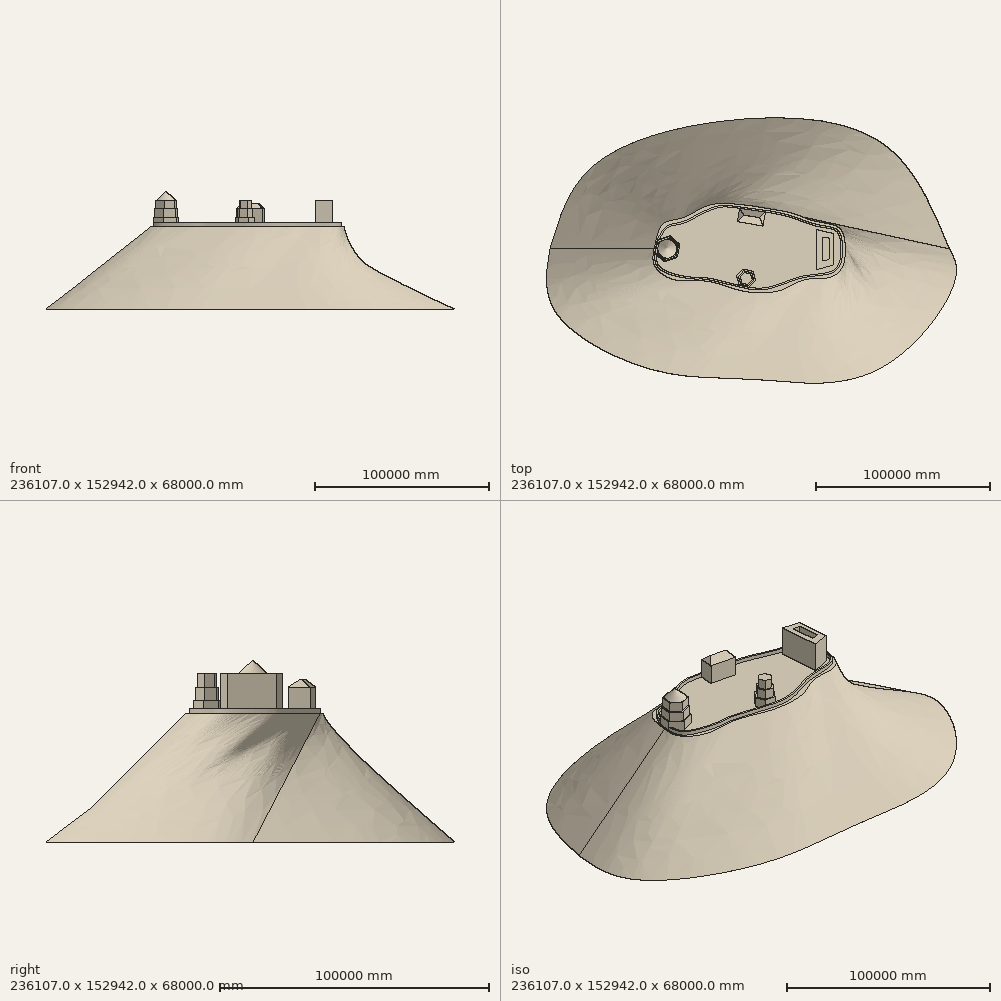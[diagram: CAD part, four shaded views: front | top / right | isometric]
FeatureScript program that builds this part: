
annotation { "Feature Type Name" : "Feature", "Feature Type Description" : "" }
export const myFeature = defineFeature(function(context is Context, id is Id, definition is map)
    precondition{}
    {
        {
            var Q0;
            Q0=qCreatedBy(makeId("Top.planeOp"),FACE);
            var sketch = newSketch(context, id + "F0", { "sketchPlane" : qUnion([Q0])});
            skFitSpline(sketch, "E0", {"points": [v(-115000, 0) * mm, v(-89790.23, 47800.29) * mm, v(0, 75000) * mm, v(78228.6, 59379.3) * mm, v(115000, 0) * mm], "startDerivative": vector(72130.1, 245823.46) * mm, "endDerivative": vector(117280.33, -283439.38) * mm});
            skFitSpline(sketch, "E1", {"points": [v(-115000, 0) * mm, v(-112209.16, -35716.4) * mm, v(-53821.4, -70207.06) * mm, v(0, -75000) * mm, v(72808.62, -70207.06) * mm, v(118631.94, -16746.53) * mm, v(115000, 0) * mm], "startDerivative": vector(-45187.79, -261735.86) * mm, "endDerivative": vector(-79154.57, 142787.81) * mm});
            skSolve(sketch);
        }
        {
            var Q0;
            Q0=qCreatedBy(makeId("Top.planeOp"),FACE);
            cPlane(context, id + "F1", {"entities" : qUnion([Q0]), "cplaneType" : CPlaneType.OFFSET, "offset" : 48000 * mm, "width" : 150 * mm, "height" : 150 * mm});
        }
        {
            var Q0;
            Q0=qCreatedBy(id+"F1.planeOp",FACE);
            var sketch = newSketch(context, id + "F2", { "sketchPlane" : qUnion([Q0])});
            skFitSpline(sketch, "E2", {"points": [v(0, 25000) * mm, v(-23615.07, 25000) * mm, v(-37680.98, 18064.81) * mm, v(-49445.19, 14484.4) * mm, v(-55000, 0) * mm], "startDerivative": vector(-85644.23, 10195.07) * mm, "endDerivative": vector(-13941.06, -73239.33) * mm});
            skFitSpline(sketch, "E3", {"points": [v(-55000, 0) * mm, v(-55000, -9189.99) * mm, v(-43801.45, -17724.95) * mm, v(-26596.06, -18402.32) * mm, v(-11016.37, -22331.11) * mm, v(0, -25000) * mm, v(18246.34, -23821.34) * mm, v(32200.32, -17724.95) * mm, v(46696.2, -16370.2) * mm, v(53605.45, -10138.32) * mm, v(55000, 0) * mm, v(51844.26, 11808.72) * mm, v(37212.9, 16008.46) * mm, v(25697.5, 20208.2) * mm, v(9846.85, 23324.13) * mm, v(0, 25000) * mm], "startDerivative": vector(-35298.95, -167696.15) * mm, "endDerivative": vector(-155833.8, 28078.38) * mm});
            skSolve(sketch);
        }
        {
            var Q0;
            Q0=makeQuery(id+"F0.imprint","IMPRINT",FACE,{"disambiguationData":[TD([[makeQuery(id+"F0.imprint","IMPRINT",EDGE,{"derivedFrom":sQuery(id+"F0.wireOp",EDGE,"E0")}),-1.0]])]});
            var Q1;
            Q1=makeQuery(id+"F2.imprint","IMPRINT",FACE,{"disambiguationData":[TD([[makeQuery(id+"F2.imprint","IMPRINT",EDGE,{"derivedFrom":sQuery(id+"F2.wireOp",EDGE,"E2")}),1.0]])]});
            loft(context, id + "F3", {"sheetProfilesArray" : [{ "sheetProfileEntities" : qUnion([Q0]) }, { "sheetProfileEntities" : qUnion([Q1]) }]});
        }
        {
            var Q0;
            Q0=makeQuery(id+"F3.opLoft","CAP_FACE",FACE,{"disambiguationData":[OSD([makeQuery(id+"F2.imprint","IMPRINT",FACE,{"disambiguationData":[TD([[makeQuery(id+"F2.imprint","IMPRINT",EDGE,{"derivedFrom":sQuery(id+"F2.wireOp",EDGE,"E2")}),1.0]])]})])],"isStart":true});
            var sketch = newSketch(context, id + "F4", { "sketchPlane" : qUnion([Q0])});
            skLineSegment(sketch, "E4", {"start": v(0, 0) * mm, "end": v(-55000, 0) * mm});
            skLineSegment(sketch, "E5", {"start": v(-55000, 0) * mm, "end": v(-47500, 0) * mm});
            skCircle(sketch, "E6.cCircle", {"center": v(-47500, 0) * mm, "radius": 6664.28 * mm, "construction": true});
            skLineSegment(sketch, "E6.0", {"start": v(-54796.66, -2444.5) * mm, "end": v(-53265.33, 5096.84) * mm});
            skLineSegment(sketch, "E6.1", {"start": v(-53265.33, 5096.84) * mm, "end": v(-45968.67, 7541.35) * mm});
            skLineSegment(sketch, "E6.2", {"start": v(-45968.67, 7541.35) * mm, "end": v(-40203.34, 2444.5) * mm});
            skLineSegment(sketch, "E6.3", {"start": v(-40203.34, 2444.5) * mm, "end": v(-41734.67, -5096.84) * mm});
            skLineSegment(sketch, "E6.4", {"start": v(-41734.67, -5096.84) * mm, "end": v(-49031.33, -7541.35) * mm});
            skLineSegment(sketch, "E6.5", {"start": v(-49031.33, -7541.35) * mm, "end": v(-54796.66, -2444.5) * mm});
            skPoint(sketch, "E6.0.midPoint", {"position": v(-54031, 1326.17) * mm});
            skSolve(sketch);
        }
        {
            var Q0;
            {var subQ0=sQuery(id+"F4.wireOp",EDGE,"E6.4");Q0=makeQuery(id+"F4.imprint","IMPRINT",FACE,{"disambiguationData":[TD([[makeQuery(id+"F4.imprint","IMPRINT",EDGE,{"derivedFrom":subQ0}),-1.0]])]});}
            var Q1;
            {var subQ0=sQuery(id+"F4.wireOp",EDGE,"E6.1");Q1=makeQuery(id+"F4.imprint","IMPRINT",FACE,{"disambiguationData":[TD([[makeQuery(id+"F4.imprint","IMPRINT",EDGE,{"derivedFrom":subQ0}),-1.0]])]});}
            extrude(context, id + "F5", {"entities" : qUnion([Q0, Q1]), "operationType" : NewBodyOperationType.ADD, "depth" : 5000 * mm});
        }
        {
            var Q0;
            Q0=makeQuery(id+"F5.opExtrude","CAP_FACE",FACE,{"disambiguationData":[OSD([sQuery(id+"F4.wireOp",EDGE,"E6.0"),sQuery(id+"F4.wireOp",EDGE,"E6.1"),sQuery(id+"F4.wireOp",EDGE,"E6.2"),sQuery(id+"F4.wireOp",EDGE,"E6.3"),sQuery(id+"F4.wireOp",EDGE,"E6.4"),sQuery(id+"F4.wireOp",EDGE,"E6.5")])],"isStart":false});
            var sketch = newSketch(context, id + "F6", { "sketchPlane" : qUnion([Q0])});
            skCircle(sketch, "E7.cCircle", {"center": v(-47581.15, 0) * mm, "radius": 6138.92 * mm, "construction": true});
            skLineSegment(sketch, "E7.0", {"start": v(-40859.7, 2251.8) * mm, "end": v(-42270.31, -4695.05) * mm});
            skLineSegment(sketch, "E7.1", {"start": v(-42270.31, -4695.05) * mm, "end": v(-48991.76, -6946.84) * mm});
            skLineSegment(sketch, "E7.2", {"start": v(-48991.76, -6946.84) * mm, "end": v(-54302.6, -2251.8) * mm});
            skLineSegment(sketch, "E7.3", {"start": v(-54302.6, -2251.8) * mm, "end": v(-52891.99, 4695.05) * mm});
            skLineSegment(sketch, "E7.4", {"start": v(-52891.99, 4695.05) * mm, "end": v(-46170.54, 6946.84) * mm});
            skLineSegment(sketch, "E7.5", {"start": v(-46170.54, 6946.84) * mm, "end": v(-40859.7, 2251.8) * mm});
            skPoint(sketch, "E7.0.midPoint", {"position": v(-41565, -1221.63) * mm});
            skSolve(sketch);
        }
        {
            var Q0;
            Q0=makeQuery(id+"F6.imprint","IMPRINT",FACE,{"disambiguationData":[TD([[makeQuery(id+"F6.imprint","IMPRINT",EDGE,{"derivedFrom":sQuery(id+"F6.wireOp",EDGE,"E7.0")}),-1.0]])]});
            extrude(context, id + "F7", {"entities" : qUnion([Q0]), "operationType" : NewBodyOperationType.ADD, "depth" : 5000 * mm});
        }
        {
            var Q0;
            Q0=makeQuery(id+"F7.opExtrude","CAP_FACE",FACE,{"disambiguationData":[OSD([sQuery(id+"F6.wireOp",EDGE,"E7.0"),sQuery(id+"F6.wireOp",EDGE,"E7.1"),sQuery(id+"F6.wireOp",EDGE,"E7.2"),sQuery(id+"F6.wireOp",EDGE,"E7.3"),sQuery(id+"F6.wireOp",EDGE,"E7.4"),sQuery(id+"F6.wireOp",EDGE,"E7.5")])],"isStart":false});
            var sketch = newSketch(context, id + "F8", { "sketchPlane" : qUnion([Q0])});
            skCircle(sketch, "E8.cCircle", {"center": v(-47481.06, 0) * mm, "radius": 5420.52 * mm, "construction": true});
            skLineSegment(sketch, "E8.0", {"start": v(-41546.18, 1988.28) * mm, "end": v(-42791.71, -4145.61) * mm});
            skLineSegment(sketch, "E8.1", {"start": v(-42791.71, -4145.61) * mm, "end": v(-48726.6, -6133.9) * mm});
            skLineSegment(sketch, "E8.2", {"start": v(-48726.6, -6133.9) * mm, "end": v(-53415.94, -1988.28) * mm});
            skLineSegment(sketch, "E8.3", {"start": v(-53415.94, -1988.28) * mm, "end": v(-52170.4, 4145.61) * mm});
            skLineSegment(sketch, "E8.4", {"start": v(-52170.4, 4145.61) * mm, "end": v(-46235.52, 6133.9) * mm});
            skLineSegment(sketch, "E8.5", {"start": v(-46235.52, 6133.9) * mm, "end": v(-41546.18, 1988.28) * mm});
            skPoint(sketch, "E8.0.midPoint", {"position": v(-42168.95, -1078.67) * mm});
            skSolve(sketch);
        }
        {
            var Q0;
            Q0=makeQuery(id+"F8.imprint","IMPRINT",FACE,{"disambiguationData":[TD([[makeQuery(id+"F8.imprint","IMPRINT",EDGE,{"derivedFrom":sQuery(id+"F8.wireOp",EDGE,"E8.0")}),-1.0]])]});
            extrude(context, id + "F9", {"entities" : qUnion([Q0]), "operationType" : NewBodyOperationType.ADD, "depth" : 5000 * mm});
        }
        {
            var Q0;
            Q0=makeQuery(id+"F3.opLoft","CAP_FACE",FACE,{"disambiguationData":[OSD([makeQuery(id+"F2.imprint","IMPRINT",FACE,{"disambiguationData":[TD([[makeQuery(id+"F2.imprint","IMPRINT",EDGE,{"derivedFrom":sQuery(id+"F2.wireOp",EDGE,"E2")}),1.0]])]})])],"isStart":true});
            var sketch = newSketch(context, id + "F10", { "sketchPlane" : qUnion([Q0])});
            skFitSpline(sketch, "E9", {"points": [v(-54796.66, -2444.5) * mm, v(-54025.04, -8683.25) * mm, v(-48181.4, -13844.42) * mm, v(-32100.73, -17384.73) * mm, v(-26814.83, -17382.16) * mm, v(-12304.75, -20499.15) * mm, v(8976.7, -23401.16) * mm, v(28547.6, -17221.27) * mm, v(42950.2, -15071.63) * mm, v(51333.8, -10879.83) * mm, v(53375.96, 3092.84) * mm, v(50151.5, 11154) * mm, v(39510.77, 13841.05) * mm, v(28169.48, 17572.49) * mm, v(16848.58, 20860.28) * mm, v(-6824.2, 24518.8) * mm, v(-17915.3, 24712.72) * mm, v(-30172.03, 19637.67) * mm, v(-39173.06, 15424.42) * mm, v(-47216.54, 13222.04) * mm, v(-53265.33, 5096.84) * mm], "startDerivative": vector(81.44, -181720.02) * mm, "endDerivative": vector(-114550.78, -214633.23) * mm});
            skFitSpline(sketch, "E10.0", {"points": [v(-54801.66, -2444.5) * mm, v(-54801.56, -2681.12) * mm, v(-54801.35, -3154.36) * mm, v(-54795.16, -3861.88) * mm, v(-54777.24, -4564.68) * mm, v(-54741.7, -5260.36) * mm, v(-54682.7, -5946.56) * mm, v(-54609.07, -6508.49) * mm, v(-54532.55, -6950.9) * mm, v(-54465.62, -7278.85) * mm, v(-54388.42, -7602.64) * mm, v(-54300.2, -7921.97) * mm, v(-54216.9, -8184.11) * mm, v(-54144.02, -8391.3) * mm, v(-54086.15, -8545.38) * mm, v(-54024.97, -8698.13) * mm, v(-53960.4, -8849.5) * mm, v(-53892.4, -8999.5) * mm, v(-53797.13, -9197.68) * mm, v(-53669.3, -9442.02) * mm, v(-53501.63, -9729.84) * mm, v(-53319.4, -10012.33) * mm, v(-53056.66, -10381.94) * mm, v(-52690.43, -10830.86) * mm, v(-52188.2, -11349) * mm, v(-51715.49, -11764) * mm, v(-51303.68, -12086.1) * mm, v(-50977.72, -12322.8) * mm, v(-50634.37, -12554.64) * mm, v(-50273.35, -12781.7) * mm, v(-49894.37, -13004.02) * mm, v(-49497.15, -13221.65) * mm, v(-49081.4, -13434.63) * mm, v(-48646.85, -13643.03) * mm, v(-48193.2, -13846.89) * mm, v(-47720.17, -14046.26) * mm, v(-47229.17, -14241.03) * mm, v(-46721.66, -14431.1) * mm, v(-46199.08, -14616.36) * mm, v(-45662.88, -14796.7) * mm, v(-45114.5, -14972.02) * mm, v(-44555.37, -15142.2) * mm, v(-43986.94, -15307.16) * mm, v(-43218.58, -15519.97) * mm, v(-42242.1, -15772.34) * mm, v(-41056.25, -16052.52) * mm, v(-39867.87, -16309.17) * mm, v(-38688.5, -16541.42) * mm, v(-37529.72, -16748.42) * mm, v(-36590.83, -16899.15) * mm, v(-35861.56, -17006.26) * mm, v(-35326.97, -17079.73) * mm, v(-34806.2, -17146.24) * mm, v(-34300.66, -17205.7) * mm, v(-33811.82, -17257.96) * mm, v(-33341.12, -17302.96) * mm, v(-32965.19, -17334.29) * mm, v(-32674.95, -17355.6) * mm, v(-32462.71, -17369.7) * mm, v(-32290.52, -17379.87) * mm, v(-32155.67, -17387.05) * mm, v(-32056, -17391.95) * mm, v(-31957.82, -17396.37) * mm, v(-31828.8, -17401.66) * mm, v(-31671.02, -17407.15) * mm, v(-31486.94, -17412.09) * mm, v(-31248.13, -17416.6) * mm, v(-30961.29, -17418.7) * mm, v(-30633.34, -17416.5) * mm, v(-30319.24, -17410.5) * mm, v(-30016.6, -17401.67) * mm, v(-29723, -17390.97) * mm, v(-29436.02, -17379.36) * mm, v(-29059.02, -17363.91) * mm, v(-28685.65, -17350.44) * mm, v(-28306.27, -17342.75) * mm, v(-28016.32, -17340.84) * mm, v(-27768.16, -17343.23) * mm, v(-27564.52, -17348.03) * mm, v(-27408.92, -17353.18) * mm, v(-27250.16, -17360) * mm, v(-27114.97, -17367.2) * mm, v(-27004.94, -17373.9) * mm, v(-26921.43, -17379.42) * mm, v(-26836.91, -17385.46) * mm, v(-26751.33, -17392.01) * mm, v(-26664.69, -17399.1) * mm, v(-26547.76, -17409.23) * mm, v(-26399, -17423.18) * mm, v(-26216.4, -17441.96) * mm, v(-25967.52, -17469.66) * mm, v(-25646.51, -17509.2) * mm, v(-25245.96, -17564.23) * mm, v(-24830.59, -17626.6) * mm, v(-24257.72, -17719.16) * mm, v(-23507.27, -17851.88) * mm, v(-22556, -18036.23) * mm, v(-21558.25, -18243.55) * mm, v(-20518.28, -18471.73) * mm, v(-19440.35, -18718.67) * mm, v(-18328.7, -18982.24) * mm, v(-17187.6, -19260.34) * mm, v(-16021.31, -19550.84) * mm, v(-15031.94, -19801.5) * mm, v(-14232.1, -20006.14) * mm, v(-13628.57, -20161.39) * mm, v(-13123.05, -20292.03) * mm, v(-12717.34, -20397.17) * mm, v(-12412.47, -20476.3) * mm, v(-12107.1, -20555.69) * mm, v(-11699.3, -20661.8) * mm, v(-11188.4, -20794.8) * mm, v(-10573.53, -20954.48) * mm, v(-9751.5, -21166.91) * mm, v(-8720.05, -21430.4) * mm, v(-7476.91, -21739.57) * mm, v(-6229.2, -22038.04) * mm, v(-4977.76, -22322.12) * mm, v(-3723.4, -22588.1) * mm, v(-2466.96, -22832.27) * mm, v(-1209.27, -23050.94) * mm, v(48.85, -23240.41) * mm, v(1306.55, -23396.98) * mm, v(2563.01, -23516.95) * mm, v(3817.4, -23596.62) * mm, v(4860.31, -23626.34) * mm, v(5692.77, -23626.26) * mm, v(6316.08, -23613.8) * mm, v(6938.24, -23588.5) * mm, v(7455.68, -23556.33) * mm, v(7868.95, -23523.7) * mm, v(8178.56, -23495.72) * mm, v(8487.8, -23464.19) * mm, v(8745.19, -23434.9) * mm, v(8950.9, -23409.62) * mm, v(9156.48, -23383.11) * mm, v(9413.21, -23347.68) * mm, v(9720.88, -23301.59) * mm, v(10130.57, -23235.5) * mm, v(10641.67, -23144.4) * mm, v(11253.33, -23022.31) * mm, v(11863.33, -22888.2) * mm, v(12674.42, -22694.34) * mm, v(13684.02, -22425.75) * mm, v(14888.59, -22067.44) * mm, v(16086.05, -21679.2) * mm, v(17276.26, -21267.08) * mm, v(18459.07, -20837.15) * mm, v(19634.34, -20395.46) * mm, v(20801.91, -19948.07) * mm, v(21961.65, -19501.04) * mm, v(23113.4, -19060.42) * mm, v(24066.4, -18703.64) * mm, v(24824.66, -18427.48) * mm, v(25391.27, -18225.75) * mm, v(25955.76, -18030.17) * mm, v(26518.13, -17841.49) * mm, v(26984.98, -17690.64) * mm, v(27357.38, -17574.17) * mm, v(27636.14, -17489.02) * mm, v(27914.35, -17406.16) * mm, v(28192, -17325.69) * mm, v(28422.93, -17260.7) * mm, v(28607.4, -17210) * mm, v(28791.68, -17160.16) * mm, v(29021.68, -17099.46) * mm, v(29297.11, -17029.11) * mm, v(29571.97, -16961.19) * mm, v(29937.67, -16873.76) * mm, v(30393.3, -16770.19) * mm, v(30937.61, -16654.51) * mm, v(31479.4, -16546.9) * mm, v(32198.3, -16413.46) * mm, v(33090.25, -16264.13) * mm, v(34149.3, -16108.59) * mm, v(35196.47, -15972.37) * mm, v(36231.17, -15851.17) * mm, v(37252.8, -15740.67) * mm, v(38260.76, -15636.56) * mm, v(39254.47, -15534.52) * mm, v(40233.34, -15430.23) * mm, v(41036.2, -15337.86) * mm, v(41670.47, -15258.52) * mm, v(42142.1, -15195.76) * mm, v(42531.66, -15140.3) * mm, v(42841.18, -15093.76) * mm, v(43072.27, -15057.7) * mm, v(43302.26, -15020.42) * mm, v(43607.35, -14968.94) * mm, v(43985.65, -14901.08) * mm, v(44434.22, -14813.28) * mm, v(45024.44, -14686.79) * mm, v(45746.26, -14509.2) * mm, v(46582.94, -14259.23) * mm, v(47386.17, -13966.64) * mm, v(48152, -13625.7) * mm, v(48876.45, -13230.7) * mm, v(49442.38, -12851.68) * mm, v(49870.47, -12515.7) * mm, v(50178.72, -12246.62) * mm, v(50473.64, -11959.72) * mm, v(50707.9, -11705.2) * mm, v(50888.15, -11491.96) * mm, v(51019.7, -11327.13) * mm, v(51147.54, -11157.31) * mm, v(51250.94, -11011.57) * mm, v(51331.74, -10892.39) * mm, v(51391.38, -10801.7) * mm, v(51450.06, -10709.72) * mm, v(51527.02, -10585.4) * mm, v(51620.86, -10426.86) * mm, v(51729.7, -10231.74) * mm, v(51834.85, -10031.9) * mm, v(51970.17, -9759.34) * mm, v(52130.3, -9407.53) * mm, v(52308.4, -8968.71) * mm, v(52472.8, -8514.38) * mm, v(52623.89, -8045.65) * mm, v(52808.08, -7403) * mm, v(53006.88, -6569.35) * mm, v(53198.15, -5529.46) * mm, v(53345.07, -4459.06) * mm, v(53450.63, -3367.18) * mm, v(53517.8, -2262.85) * mm, v(53549.55, -1155.07) * mm, v(53548.85, -52.88) * mm, v(53523.7, 853.44) * mm, v(53490.31, 1566.68) * mm, v(53459.02, 2094.58) * mm, v(53428.03, 2527.7) * mm, v(53400.49, 2869.54) * mm, v(53378.5, 3123.46) * mm, v(53355.21, 3374.78) * mm, v(53322.33, 3706.38) * mm, v(53277.6, 4114.23) * mm, v(53217.5, 4592.73) * mm, v(53127.99, 5215.81) * mm, v(52997.01, 5965.97) * mm, v(52804.43, 6818.04) * mm, v(52571.57, 7619.76) * mm, v(52293.55, 8368.88) * mm, v(52020.17, 8947.47) * mm, v(51774, 9381.8) * mm, v(51575.05, 9693) * mm, v(51361.14, 9989.37) * mm, v(51131.68, 10270.62) * mm, v(50927, 10492.16) * mm, v(50754.87, 10661.56) * mm, v(50621.5, 10784.65) * mm, v(50483.8, 10903.74) * mm, v(50341.67, 11018.81) * mm, v(50219.49, 11111.32) * mm, v(50119.45, 11183.28) * mm, v(50017.9, 11253.87) * mm, v(49888.14, 11339.6) * mm, v(49728.04, 11438.57) * mm, v(49563.65, 11533.76) * mm, v(49338.9, 11655.8) * mm, v(49047.83, 11799.48) * mm, v(48683.18, 11958.69) * mm, v(48304.04, 12105.64) * mm, v(47780.4, 12286.52) * mm, v(47094.07, 12486.78) * mm, v(46226.66, 12693.4) * mm, v(45322.5, 12874) * mm, v(44388.61, 13036.2) * mm, v(43432.07, 13187.68) * mm, v(42459.91, 13336.07) * mm, v(41479.2, 13489.03) * mm, v(40660.7, 13626.65) * mm, v(40008.67, 13746.68) * mm, v(39521.92, 13842.61) * mm, v(39038.32, 13945.43) * mm, v(38397.73, 14091.23) * mm, v(37604.84, 14288.86) * mm, v(36665.88, 14547.6) * mm, v(35739.36, 14824.95) * mm, v(34825.21, 15117.89) * mm, v(33923.37, 15423.4) * mm, v(33033.77, 15738.47) * mm, v(32156.35, 16060.11) * mm, v(31435.27, 16331.11) * mm, v(30864.42, 16548.18) * mm, v(30439.29, 16710.74) * mm, v(30017.15, 16872.7) * mm, v(29598, 17033.65) * mm, v(29181.84, 17193.24) * mm, v(28837.5, 17324.78) * mm, v(28563.53, 17428.95) * mm, v(28358.78, 17506.5) * mm, v(28154.77, 17583.43) * mm, v(27951.5, 17659.7) * mm, v(27748.86, 17735.3) * mm, v(27479.41, 17835.25) * mm, v(27143.74, 17958.62) * mm, v(26742.03, 18104.24) * mm, v(26340.7, 18247.54) * mm, v(25938.99, 18388.63) * mm, v(25401.91, 18573.9) * mm, v(24726, 18800.45) * mm, v(23901.76, 19065) * mm, v(23058.51, 19323.05) * mm, v(22190.41, 19575.37) * mm, v(21441.42, 19781.53) * mm, v(20823.95, 19944.38) * mm, v(20350.99, 20065.59) * mm, v(19867.42, 20185.95) * mm, v(19372.53, 20305.58) * mm, v(18865.58, 20424.57) * mm, v(18345.84, 20543.02) * mm, v(17901.45, 20641.36) * mm, v(17538.82, 20719.86) * mm, v(17263.19, 20778.66) * mm, v(17030.37, 20827.6) * mm, v(16842.2, 20866.74) * mm, v(16652.74, 20905.86) * mm, v(16413.53, 20954.73) * mm, v(16122.75, 21013.33) * mm, v(15828.37, 21071.86) * mm, v(15431.2, 21149.8) * mm, v(14926.29, 21247.05) * mm, v(14307.7, 21363.38) * mm, v(13677.33, 21479.28) * mm, v(13036.02, 21594.7) * mm, v(12167.54, 21747.89) * mm, v(11058.99, 21937.86) * mm, v(9698.97, 22162.96) * mm, v(8316.2, 22384.71) * mm, v(6917.63, 22602.65) * mm, v(5510.27, 22816.3) * mm, v(4101.1, 23025.2) * mm, v(2697.08, 23228.88) * mm, v(1305.2, 23426.85) * mm, v(-67.53, 23618.65) * mm, v(-1189.73, 23772.95) * mm, v(-2070.94, 23892.83) * mm, v(-2722.7, 23980.9) * mm, v(-3364.44, 24067.08) * mm, v(-3995.29, 24151.3) * mm, v(-4614.37, 24233.51) * mm, v(-5220.82, 24313.65) * mm, v(-5714.94, 24378.65) * mm, v(-6103.04, 24429.55) * mm, v(-6390.41, 24467.18) * mm, v(-6626.7, 24498.06) * mm, v(-6813.79, 24522.48) * mm, v(-6999.54, 24546.72) * mm, v(-7229.27, 24576.63) * mm, v(-7501.13, 24611.9) * mm, v(-7769.28, 24646.47) * mm, v(-8122.02, 24691.59) * mm, v(-8554.23, 24746.04) * mm, v(-9059.82, 24807.9) * mm, v(-9553.23, 24865.9) * mm, v(-10035.36, 24919.69) * mm, v(-10664.31, 24985.28) * mm, v(-11426.7, 25054.87) * mm, v(-12310.55, 25115.61) * mm, v(-13170.47, 25150.62) * mm, v(-14013.52, 25156.96) * mm, v(-14707.9, 25135.9) * mm, v(-15262.05, 25101.75) * mm, v(-15677.87, 25067.14) * mm, v(-16094.76, 25023.14) * mm, v(-16513.63, 24969.4) * mm, v(-16865.07, 24916.19) * mm, v(-17148.09, 24868.38) * mm, v(-17361.4, 24829.85) * mm, v(-17575.86, 24788.61) * mm, v(-17755.63, 24751.95) * mm, v(-17900.14, 24721.21) * mm, v(-18045.13, 24689.53) * mm, v(-18227.24, 24648.18) * mm, v(-18447.14, 24595.82) * mm, v(-18668.33, 24540.76) * mm, v(-18890.78, 24483.08) * mm, v(-19188.95, 24402.74) * mm, v(-19564.48, 24296.04) * mm, v(-20019.2, 24158.43) * mm, v(-20477.52, 24011.72) * mm, v(-20939, 23856.39) * mm, v(-21403.2, 23692.9) * mm, v(-22025.12, 23464.67) * mm, v(-22807, 23161.36) * mm, v(-23748.83, 22772.31) * mm, v(-24690.56, 22361.98) * mm, v(-25628.58, 21934.13) * mm, v(-26559.24, 21492.54) * mm, v(-27478.92, 21040.98) * mm, v(-28233.13, 20659.52) * mm, v(-28827.36, 20353.14) * mm, v(-29268.02, 20123.23) * mm, v(-29630.67, 19931.92) * mm, v(-29917.83, 19779.27) * mm, v(-30131.66, 19665.05) * mm, v(-30343.89, 19551.15) * mm, v(-30624.76, 19399.78) * mm, v(-30972.07, 19211.59) * mm, v(-31383.2, 18987.75) * mm, v(-31924.37, 18692.4) * mm, v(-32588.78, 18329.93) * mm, v(-33370.07, 17908.44) * mm, v(-34138.66, 17503.19) * mm, v(-34897.85, 17116.94) * mm, v(-35650.93, 16752.47) * mm, v(-36276.16, 16469.18) * mm, v(-36776.59, 16256.2) * mm, v(-37152.44, 16103.63) * mm, v(-37529.25, 15958.57) * mm, v(-37907.41, 15821.37) * mm, v(-38224.03, 15713.87) * mm, v(-38478.4, 15632.14) * mm, v(-38669.8, 15573.03) * mm, v(-38861.83, 15516.14) * mm, v(-39022.44, 15470.62) * mm, v(-39151.3, 15435.35) * mm, v(-39248.16, 15409.5) * mm, v(-39345.2, 15384.2) * mm, v(-39474.82, 15351.2) * mm, v(-39637.29, 15311.28) * mm, v(-39832.87, 15265.3) * mm, v(-40029, 15221.12) * mm, v(-40291.16, 15164.36) * mm, v(-40619.88, 15097.04) * mm, v(-41015.43, 15020.76) * mm, v(-41411.51, 14947.66) * mm, v(-41807.55, 14876.44) * mm, v(-42202.98, 14805.78) * mm, v(-42728.67, 14710.58) * mm, v(-43381.47, 14586.42) * mm, v(-44024.76, 14446.64) * mm, v(-44531.43, 14320.2) * mm, v(-44906.9, 14216.75) * mm, v(-45277.27, 14103.35) * mm, v(-45641.97, 13978.71) * mm, v(-46000.44, 13841.5) * mm, v(-46293.51, 13715.6) * mm, v(-46524.29, 13607.27) * mm, v(-46695.46, 13522.07) * mm, v(-46864.65, 13432.73) * mm, v(-47031.8, 13339.11) * mm, v(-47169.3, 13257.38) * mm, v(-47278.22, 13189.68) * mm, v(-47386.4, 13120.45) * mm, v(-47520.28, 13031.07) * mm, v(-47678.8, 12919.35) * mm, v(-47835.26, 12803.28) * mm, v(-48041.16, 12642.85) * mm, v(-48293.59, 12431.92) * mm, v(-48588.95, 12162.98) * mm, v(-48877.16, 11879) * mm, v(-49158.57, 11580.78) * mm, v(-49525.25, 11165.22) * mm, v(-49968.51, 10614.12) * mm, v(-50479.32, 9908.5) * mm, v(-50972.03, 9164.93) * mm, v(-51449.67, 8389.73) * mm, v(-51915.25, 7589.22) * mm, v(-52523.96, 6496.58) * mm, v(-52971.43, 5658.14) * mm, v(-53269.74, 5099.2) * mm]});
            skFitSpline(sketch, "E11.0", {"points": [v(-53801.66, -2444.06) * mm, v(-53801.56, -2680.67) * mm, v(-53801.34, -3151.16) * mm, v(-53796.25, -3730.38) * mm, v(-53786.52, -4187.1) * mm, v(-53775.73, -4525.97) * mm, v(-53760.77, -4860.83) * mm, v(-53741.03, -5191.32) * mm, v(-53715.88, -5517.09) * mm, v(-53684.72, -5837.8) * mm, v(-53646.99, -6153.09) * mm, v(-53602.13, -6462.64) * mm, v(-53549.62, -6766.14) * mm, v(-53488.94, -7063.32) * mm, v(-53419.63, -7353.92) * mm, v(-53354.26, -7590.44) * mm, v(-53297.18, -7776.2) * mm, v(-53251.9, -7913.8) * mm, v(-53212.08, -8027) * mm, v(-53178.93, -8116.68) * mm, v(-53153.42, -8183.5) * mm, v(-53131.6, -8238.83) * mm, v(-53113.82, -8282.88) * mm, v(-53100.31, -8315.8) * mm, v(-53086.63, -8348.64) * mm, v(-53068.15, -8392.3) * mm, v(-53044.6, -8446.69) * mm, v(-53015.6, -8511.62) * mm, v(-52985.87, -8576.23) * mm, v(-52955.4, -8640.52) * mm, v(-52913.79, -8725.84) * mm, v(-52859.9, -8831.74) * mm, v(-52769.6, -8999.62) * mm, v(-52648.98, -9206.7) * mm, v(-52491.34, -9451.1) * mm, v(-52320.3, -9691.72) * mm, v(-52135.33, -9928.84) * mm, v(-51935.87, -10162.68) * mm, v(-51721.36, -10393.42) * mm, v(-51491.25, -10621.17) * mm, v(-51245, -10846.02) * mm, v(-50982.1, -11067.99) * mm, v(-50702.03, -11287.08) * mm, v(-50404.35, -11503.26) * mm, v(-50088.62, -11716.48) * mm, v(-49754.44, -11926.69) * mm, v(-49401.43, -12133.8) * mm, v(-49091.27, -12303.74) * mm, v(-48833.39, -12438.07) * mm, v(-48635.06, -12538) * mm, v(-48431.78, -12637.1) * mm, v(-48258.21, -12718.98) * mm, v(-48116.85, -12784.07) * mm, v(-48009.56, -12832.67) * mm, v(-47919.1, -12872.99) * mm, v(-47846.1, -12905.14) * mm, v(-47791.03, -12929.2) * mm, v(-47735.64, -12953.2) * mm, v(-47661.34, -12985.15) * mm, v(-47567.64, -13024.96) * mm, v(-47453.92, -13072.53) * mm, v(-47300.62, -13135.69) * mm, v(-47105.9, -13214.1) * mm, v(-46867.54, -13307.3) * mm, v(-46624.66, -13399.58) * mm, v(-46295.1, -13521.33) * mm, v(-45872.88, -13671.01) * mm, v(-45351.45, -13846.4) * mm, v(-44816.83, -14017.32) * mm, v(-44270.58, -14183.59) * mm, v(-43714.28, -14345.03) * mm, v(-42961.17, -14553.6) * mm, v(-42002.32, -14801.44) * mm, v(-40835.91, -15077.03) * mm, v(-39665.77, -15329.74) * mm, v(-38503.92, -15558.55) * mm, v(-37552.62, -15728.48) * mm, v(-36807.74, -15851.51) * mm, v(-36258.68, -15937.2) * mm, v(-35720.73, -16016.2) * mm, v(-35195.42, -16088.4) * mm, v(-34684.3, -16153.69) * mm, v(-34188.9, -16211.94) * mm, v(-33790.52, -16254.54) * mm, v(-33481.28, -16285) * mm, v(-33254.29, -16306.02) * mm, v(-33032.45, -16325.2) * mm, v(-32815.97, -16342.55) * mm, v(-32640.22, -16355.46) * mm, v(-32502.53, -16364.85) * mm, v(-32400.73, -16371.43) * mm, v(-32300.45, -16377.54) * mm, v(-32218.15, -16382.24) * mm, v(-32153.1, -16385.77) * mm, v(-32104.72, -16388.3) * mm, v(-32056.72, -16390.7) * mm, v(-32009.12, -16393) * mm, v(-31961.89, -16395.17) * mm, v(-31915, -16397.24) * mm, v(-31868.48, -16399.2) * mm, v(-31806.92, -16401.65) * mm, v(-31730.82, -16404.46) * mm, v(-31610.83, -16408.4) * mm, v(-31464.05, -16412.34) * mm, v(-31292.7, -16415.58) * mm, v(-31125.79, -16417.47) * mm, v(-30908.65, -16418.32) * mm, v(-30646.46, -16416.55) * mm, v(-30343.7, -16410.78) * mm, v(-30049.82, -16402.22) * mm, v(-29761.97, -16391.73) * mm, v(-29477.32, -16380.21) * mm, v(-29193.22, -16368.57) * mm, v(-28907.16, -16357.78) * mm, v(-28616.84, -16348.84) * mm, v(-28320.13, -16342.82) * mm, v(-28065.92, -16341.13) * mm, v(-27857.46, -16342.31) * mm, v(-27698.33, -16344.6) * mm, v(-27536.22, -16348.41) * mm, v(-27370.88, -16353.89) * mm, v(-27230.24, -16359.94) * mm, v(-27115.9, -16365.73) * mm, v(-27029.2, -16370.57) * mm, v(-26956.13, -16375.02) * mm, v(-26897.17, -16378.84) * mm, v(-26852.7, -16381.84) * mm, v(-26807.98, -16384.98) * mm, v(-26770.48, -16387.7) * mm, v(-26740.36, -16389.95) * mm, v(-26710.16, -16392.24) * mm, v(-26672.26, -16395.2) * mm, v(-26626.56, -16398.87) * mm, v(-26565.33, -16403.95) * mm, v(-26457.4, -16413.3) * mm, v(-26301, -16427.98) * mm, v(-26109.8, -16447.64) * mm, v(-25915.08, -16469.32) * mm, v(-25716.87, -16492.96) * mm, v(-25447.98, -16527.07) * mm, v(-25103.3, -16574.43) * mm, v(-24676.28, -16638.55) * mm, v(-24236.2, -16709.67) * mm, v(-23783.42, -16787.51) * mm, v(-23163.34, -16899.91) * mm, v(-22358.55, -17055.88) * mm, v(-21348.9, -17265.69) * mm, v(-20299.1, -17496.04) * mm, v(-19213.04, -17744.84) * mm, v(-18094.72, -18010) * mm, v(-16948.16, -18289.42) * mm, v(-15972.6, -18532.42) * mm, v(-15182.15, -18731.85) * mm, v(-14584.84, -18883.69) * mm, v(-13983.57, -19037.51) * mm, v(-13479.65, -19167.14) * mm, v(-13075.07, -19271.58) * mm, v(-12770.97, -19350.24) * mm, v(-12517.05, -19416.04) * mm, v(-12313.66, -19468.81) * mm, v(-12160.98, -19508.46) * mm, v(-12008.2, -19548.16) * mm, v(-11855.33, -19587.91) * mm, v(-11702.37, -19627.7) * mm, v(-11498.33, -19680.8) * mm, v(-11243.09, -19747.23) * mm, v(-10936.5, -19826.99) * mm, v(-10629.64, -19906.73) * mm, v(-10220.12, -20012.95) * mm, v(-9707.6, -20145.4) * mm, v(-9091.63, -20303.36) * mm, v(-8474.84, -20459.88) * mm, v(-7857.34, -20614.49) * mm, v(-7033.2, -20817.5) * mm, v(-6001.76, -21064.23) * mm, v(-4762.9, -21345.44) * mm, v(-3523.83, -21608.16) * mm, v(-2285.43, -21848.82) * mm, v(-1048.63, -22063.84) * mm, v(185.62, -22249.7) * mm, v(1416.4, -22402.9) * mm, v(2642.8, -22519.97) * mm, v(3660.4, -22584.58) * mm, v(4471.4, -22614.8) * mm, v(5078, -22626.3) * mm, v(5682.88, -22626.24) * mm, v(6285.91, -22614.2) * mm, v(6887.02, -22589.75) * mm, v(7386.27, -22558.7) * mm, v(7784.63, -22527.24) * mm, v(8033.16, -22504.78) * mm, v(8231.71, -22485.11) * mm, v(8380.49, -22469.5) * mm, v(8529.13, -22453.02) * mm, v(8652.88, -22438.57) * mm, v(8751.82, -22426.56) * mm, v(8825.97, -22417.34) * mm, v(8900.11, -22407.89) * mm, v(8998.95, -22395) * mm, v(9122.48, -22378.32) * mm, v(9320.12, -22350.46) * mm, v(9567.11, -22313.46) * mm, v(9863.42, -22265.66) * mm, v(10159.65, -22214.53) * mm, v(10455.8, -22160.17) * mm, v(10751.85, -22102.67) * mm, v(11146.47, -22021.9) * mm, v(11639.5, -21913.5) * mm, v(12230.74, -21772.21) * mm, v(12821.52, -21620.38) * mm, v(13411.8, -21458.73) * mm, v(14001.54, -21287.96) * mm, v(14787.1, -21049.07) * mm, v(15767.48, -20731.23) * mm, v(16941.13, -20324.87) * mm, v(18111.67, -19899.41) * mm, v(19278.85, -19460.77) * mm, v(20442.48, -19014.9) * mm, v(21602.45, -18567.78) * mm, v(22565.97, -18199.16) * mm, v(23334.93, -17909.7) * mm, v(23910.74, -17696.07) * mm, v(24485.63, -17486.7) * mm, v(25059.65, -17282.32) * mm, v(25632.8, -17083.74) * mm, v(26109.72, -16923.72) * mm, v(26490.86, -16799.38) * mm, v(26776.52, -16708.07) * mm, v(27062, -16618.79) * mm, v(27347.27, -16531.64) * mm, v(27584.86, -16460.88) * mm, v(27774.84, -16405.44) * mm, v(27917.28, -16364.45) * mm, v(28035.94, -16330.8) * mm, v(28130.86, -16304.2) * mm, v(28202.03, -16284.4) * mm, v(28273.2, -16264.77) * mm, v(28344.33, -16245.3) * mm, v(28415.44, -16225.99) * mm, v(28510.18, -16200.47) * mm, v(28628.49, -16168.99) * mm, v(28770.29, -16131.87) * mm, v(28911.9, -16095.4) * mm, v(29100.5, -16047.62) * mm, v(29335.77, -15989.47) * mm, v(29711.21, -15899.71) * mm, v(30178.62, -15793.47) * mm, v(30736.36, -15674.94) * mm, v(31290.84, -15564.81) * mm, v(31841.96, -15462.52) * mm, v(32389.6, -15367.5) * mm, v(33115.05, -15249.74) * mm, v(34012.69, -15117.92) * mm, v(35074.39, -14979.82) * mm, v(36119.85, -14857.37) * mm, v(37148.32, -14746.14) * mm, v(38159.02, -14641.75) * mm, v(38985.83, -14556.84) * mm, v(39637.6, -14488.04) * mm, v(40121.52, -14435.46) * mm, v(40600.4, -14381.4) * mm, v(41074.15, -14325.32) * mm, v(41464.6, -14276.48) * mm, v(41774.29, -14235.9) * mm, v(42005.21, -14204.63) * mm, v(42234.79, -14172.48) * mm, v(42424.95, -14144.9) * mm, v(42576.4, -14122.33) * mm, v(42727.4, -14099.41) * mm, v(42877.68, -14075.96) * mm, v(43027.2, -14051.95) * mm, v(43176.18, -14027.55) * mm, v(43361.4, -13996.3) * mm, v(43581.96, -13957.53) * mm, v(43873.69, -13904) * mm, v(44233.76, -13833.52) * mm, v(44657.97, -13742.6) * mm, v(45073.74, -13644.76) * mm, v(45480.52, -13539.44) * mm, v(45877.79, -13426.1) * mm, v(46265.02, -13304.24) * mm, v(46641.72, -13173.36) * mm, v(47007.44, -13032.97) * mm, v(47361.77, -12882.63) * mm, v(47704.33, -12721.88) * mm, v(48034.83, -12550.25) * mm, v(48353.03, -12367.28) * mm, v(48658.78, -12172.46) * mm, v(48952, -11965.22) * mm, v(49232.67, -11744.91) * mm, v(49500.81, -11510.8) * mm, v(49713.9, -11303.51) * mm, v(49878.16, -11129.87) * mm, v(49998.27, -10995.6) * mm, v(50115.3, -10857.17) * mm, v(50210.23, -10738.2) * mm, v(50284.64, -10640.8) * mm, v(50339.67, -10566.62) * mm, v(50384.88, -10503.83) * mm, v(50420.65, -10453.02) * mm, v(50447.3, -10414.6) * mm, v(50469.33, -10382.35) * mm, v(50486.86, -10356.4) * mm, v(50499.95, -10336.86) * mm, v(50513, -10317.24) * mm, v(50530.35, -10290.96) * mm, v(50560.57, -10244.67) * mm, v(50603.32, -10177.65) * mm, v(50670.86, -10068.55) * mm, v(50753.64, -9928.7) * mm, v(50850.3, -9755.45) * mm, v(50944.28, -9576.87) * mm, v(51035.52, -9393.1) * mm, v(51124.03, -9204.26) * mm, v(51238.34, -8945.92) * mm, v(51374.28, -8611.06) * mm, v(51526.2, -8191.34) * mm, v(51666.89, -7754.95) * mm, v(51796.4, -7303.18) * mm, v(51914.81, -6837.28) * mm, v(52022.27, -6358.55) * mm, v(52118.96, -5868.24) * mm, v(52205.08, -5367.64) * mm, v(52280.86, -4858) * mm, v(52368.46, -4168.11) * mm, v(52453.45, -3289.4) * mm, v(52518.61, -2218.69) * mm, v(52544.36, -1320.98) * mm, v(52549.17, -604.37) * mm, v(52545.24, -68.9) * mm, v(52534.1, 463.41) * mm, v(52516.14, 991.34) * mm, v(52495.77, 1426.65) * mm, v(52476.4, 1771.52) * mm, v(52460.4, 2028.33) * mm, v(52442.97, 2283.16) * mm, v(52427.27, 2493.73) * mm, v(52414.05, 2661.04) * mm, v(52403.8, 2785.95) * mm, v(52394.98, 2889.52) * mm, v(52387.77, 2972.06) * mm, v(52382.29, 3033.8) * mm, v(52376.72, 3095.37) * mm, v(52369.2, 3177.2) * mm, v(52359.6, 3279.02) * mm, v(52347.76, 3400.43) * mm, v(52335.6, 3521.07) * mm, v(52323.08, 3640.93) * mm, v(52305.93, 3799.7) * mm, v(52283.61, 3996.2) * mm, v(52255.34, 4228.77) * mm, v(52215.58, 4534.54) * mm, v(52161.85, 4908.48) * mm, v(52090.47, 5343.57) * mm, v(52011.75, 5764.62) * mm, v(51925.27, 6171.24) * mm, v(51830.66, 6563.04) * mm, v(51727.6, 6939.65) * mm, v(51615.76, 7300.74) * mm, v(51494.9, 7646.03) * mm, v(51364.77, 7975.3) * mm, v(51225.17, 8288.4) * mm, v(51075.88, 8585.32) * mm, v(50916.67, 8866.13) * mm, v(50747.22, 9131.07) * mm, v(50597.16, 9338.9) * mm, v(50471.53, 9497.65) * mm, v(50374.43, 9613) * mm, v(50274.35, 9724.72) * mm, v(50171.18, 9832.89) * mm, v(50064.81, 9937.56) * mm, v(49973.4, 10021.94) * mm, v(49898.5, 10087.77) * mm, v(49841.46, 10136.3) * mm, v(49783.5, 10184.01) * mm, v(49724.6, 10230.9) * mm, v(49674.72, 10269.3) * mm, v(49639.39, 10295.83) * mm, v(49619.07, 10310.89) * mm, v(49603.78, 10322.13) * mm, v(49588.42, 10333.32) * mm, v(49572.99, 10344.47) * mm, v(49557.49, 10355.57) * mm, v(49541.92, 10366.63) * mm, v(49526.27, 10377.64) * mm, v(49505.3, 10392.28) * mm, v(49478.89, 10410.49) * mm, v(49446.87, 10432.19) * mm, v(49403.76, 10460.91) * mm, v(49349.09, 10496.44) * mm, v(49282.21, 10538.48) * mm, v(49214.08, 10579.92) * mm, v(49144.68, 10620.78) * mm, v(49050.48, 10674.46) * mm, v(48881.26, 10766.36) * mm, v(48627.19, 10891.85) * mm, v(48303.17, 11033.39) * mm, v(47960.85, 11166.13) * mm, v(47601.14, 11290.43) * mm, v(47225.05, 11406.72) * mm, v(46833.63, 11515.51) * mm, v(46427.93, 11617.4) * mm, v(46009.03, 11713.05) * mm, v(45578, 11803.17) * mm, v(45135.88, 11888.54) * mm, v(44683.7, 11969.96) * mm, v(44222.48, 12048.28) * mm, v(43753.2, 12124.36) * mm, v(43276.86, 12199.1) * mm, v(42794.37, 12273.44) * mm, v(42306.7, 12348.29) * mm, v(41814.74, 12424.6) * mm, v(41401.96, 12490.24) * mm, v(41070.48, 12544.46) * mm, v(40821.36, 12586.11) * mm, v(40571.82, 12628.87) * mm, v(40321.99, 12672.86) * mm, v(40113.63, 12710.66) * mm, v(39946.9, 12741.65) * mm, v(39821.85, 12765.27) * mm, v(39696.8, 12789.3) * mm, v(39592.6, 12809.69) * mm, v(39509.25, 12826.21) * mm, v(39446.75, 12838.72) * mm, v(39394.68, 12849.24) * mm, v(39353.02, 12857.7) * mm, v(39321.78, 12864.1) * mm, v(39290.56, 12870.5) * mm, v(39248.94, 12879.09) * mm, v(39196.95, 12889.89) * mm, v(39134.63, 12902.95) * mm, v(39051.6, 12920.52) * mm, v(38947.98, 12942.74) * mm, v(38823.87, 12969.82) * mm, v(38700, 12997.32) * mm, v(38535.15, 13034.52) * mm, v(38329.69, 13082.02) * mm, v(38084.1, 13140.56) * mm, v(37839.45, 13200.6) * mm, v(37595.76, 13262.08) * mm, v(37272.12, 13345.92) * mm, v(36869.94, 13454.08) * mm, v(36391.13, 13588.84) * mm, v(35916.1, 13728.19) * mm, v(35444.85, 13871.72) * mm, v(34977.37, 14019.03) * mm, v(34359.08, 14219.96) * mm, v(33595.59, 14478.6) * mm, v(32694.32, 14797.83) * mm, v(31807.93, 15122.76) * mm, v(31081.63, 15395.72) * mm, v(30508, 15613.85) * mm, v(30081.5, 15776.94) * mm, v(29658.7, 15939.15) * mm, v(29239.61, 16100.08) * mm, v(28893.48, 16232.81) * mm, v(28618.44, 16337.98) * mm, v(28413.1, 16416.3) * mm, v(28208.7, 16494.02) * mm, v(28039.13, 16558.25) * mm, v(27903.96, 16609.27) * mm, v(27802.81, 16647.37) * mm, v(27701.89, 16685.28) * mm, v(27567.58, 16735.6) * mm, v(27400.16, 16798.06) * mm, v(27133.15, 16897.1) * mm, v(26800.78, 17019.26) * mm, v(26403.43, 17163.3) * mm, v(26006.81, 17304.92) * mm, v(25610.19, 17444.22) * mm, v(25080.32, 17627.02) * mm, v(24414.18, 17850.29) * mm, v(23602.6, 18110.77) * mm, v(22772.67, 18364.74) * mm, v(21918.26, 18613.08) * mm, v(21180.74, 18816.08) * mm, v(20572.36, 18976.54) * mm, v(20106.14, 19096.02) * mm, v(19629.22, 19214.73) * mm, v(19140.86, 19332.78) * mm, v(18640.29, 19450.27) * mm, v(18126.77, 19567.3) * mm, v(17687.43, 19664.53) * mm, v(17328.73, 19742.17) * mm, v(17056, 19800.35) * mm, v(16825.58, 19848.8) * mm, v(16639.3, 19887.54) * mm, v(16498.58, 19916.6) * mm, v(16356.9, 19945.65) * mm, v(16166.67, 19984.38) * mm, v(15926.5, 20032.77) * mm, v(15634.6, 20090.8) * mm, v(15240.6, 20168.14) * mm, v(14739.4, 20264.66) * mm, v(14124.95, 20380.22) * mm, v(13498.4, 20495.42) * mm, v(12860.66, 20610.2) * mm, v(11996.6, 20762.6) * mm, v(10893.04, 20951.72) * mm, v(9538.28, 21175.95) * mm, v(8160.13, 21396.96) * mm, v(6765.68, 21614.26) * mm, v(5361.97, 21827.36) * mm, v(3956.05, 22035.78) * mm, v(2554.94, 22239.03) * mm, v(1165.65, 22436.64) * mm, v(-204.8, 22628.12) * mm, v(-1325.3, 22782.18) * mm, v(-2205.29, 22901.9) * mm, v(-2856.2, 22989.86) * mm, v(-3497.14, 23075.93) * mm, v(-4127.26, 23160.05) * mm, v(-4745.68, 23242.17) * mm, v(-5250.55, 23308.88) * mm, v(-5647.73, 23361.2) * mm, v(-5942.14, 23399.88) * mm, v(-6232.97, 23438.03) * mm, v(-6472.26, 23469.36) * mm, v(-6661.8, 23494.14) * mm, v(-6779.45, 23509.51) * mm, v(-6873.08, 23521.74) * mm, v(-6943.07, 23530.87) * mm, v(-7012.8, 23539.97) * mm, v(-7105.42, 23552.05) * mm, v(-7220.55, 23567.05) * mm, v(-7403.4, 23590.84) * mm, v(-7719.83, 23631.88) * mm, v(-8162, 23688.72) * mm, v(-8677.66, 23753.68) * mm, v(-9179.14, 23815.04) * mm, v(-9667.29, 23872.42) * mm, v(-10142.9, 23925.48) * mm, v(-10606.84, 23973.86) * mm, v(-11059.92, 24017.22) * mm, v(-11503, 24055.22) * mm, v(-11936.93, 24087.55) * mm, v(-12362.61, 24113.88) * mm, v(-12780.94, 24133.9) * mm, v(-13192.84, 24147.3) * mm, v(-13599.26, 24153.77) * mm, v(-14001.17, 24153.01) * mm, v(-14399.57, 24144.72) * mm, v(-14795.47, 24128.58) * mm, v(-15189.91, 24104.28) * mm, v(-15583.95, 24071.47) * mm, v(-15978.66, 24029.82) * mm, v(-16375.1, 23978.96) * mm, v(-16707.8, 23928.58) * mm, v(-16975.9, 23883.3) * mm, v(-17178.08, 23846.77) * mm, v(-17347.58, 23814.18) * mm, v(-17483.87, 23786.78) * mm, v(-17569.35, 23769.1) * mm, v(-17637.92, 23754.61) * mm, v(-17689.43, 23743.58) * mm, v(-17741.06, 23732.38) * mm, v(-17810.04, 23717.2) * mm, v(-17896.56, 23697.8) * mm, v(-18035.58, 23665.86) * mm, v(-18210.45, 23624.21) * mm, v(-18421.98, 23571.56) * mm, v(-18635.1, 23516.3) * mm, v(-18849.77, 23458.46) * mm, v(-19065.89, 23398.1) * mm, v(-19355.9, 23314.36) * mm, v(-19721.7, 23203.66) * mm, v(-20165.37, 23061.65) * mm, v(-20762.48, 22860.67) * mm, v(-21517.93, 22588.78) * mm, v(-22434.76, 22233.14) * mm, v(-23357.78, 21851.88) * mm, v(-24282.98, 21448.76) * mm, v(-25206.45, 21027.55) * mm, v(-26124.28, 20592.05) * mm, v(-26881.27, 20220.38) * mm, v(-27480.25, 19919.67) * mm, v(-27925.7, 19692.93) * mm, v(-28366.9, 19465.46) * mm, v(-28730.65, 19275.67) * mm, v(-29019.06, 19123.95) * mm, v(-29198.18, 19029.21) * mm, v(-29340.78, 18953.51) * mm, v(-29447.37, 18896.78) * mm, v(-29553.6, 18840.11) * mm, v(-29659.43, 18783.5) * mm, v(-29764.9, 18726.97) * mm, v(-29905.07, 18651.67) * mm, v(-30079.42, 18557.7) * mm, v(-30287.35, 18445.24) * mm, v(-30494.04, 18333.11) * mm, v(-30699.53, 18221.36) * mm, v(-30972, 18072.92) * mm, v(-31309.9, 17888.52) * mm, v(-31711.53, 17669.39) * mm, v(-32109.72, 17452.74) * mm, v(-32504.95, 17238.91) * mm, v(-33028.55, 16958.02) * mm, v(-33677.88, 16615.64) * mm, v(-34452.37, 16221.58) * mm, v(-35096.86, 15909.63) * mm, v(-35613.68, 15671.46) * mm, v(-36002.33, 15498.92) * mm, v(-36392.46, 15332.87) * mm, v(-36784.49, 15173.73) * mm, v(-37178.83, 15021.91) * mm, v(-37509.7, 14901.86) * mm, v(-37775.96, 14809.91) * mm, v(-37976.47, 14743.06) * mm, v(-38177.85, 14678.36) * mm, v(-38346.44, 14626.29) * mm, v(-38481.78, 14585.76) * mm, v(-38583.53, 14555.95) * mm, v(-38668.54, 14531.58) * mm, v(-38736.67, 14512.38) * mm, v(-38787.83, 14498.14) * mm, v(-38830.52, 14486.38) * mm, v(-38864.7, 14477.06) * mm, v(-38890.37, 14470.1) * mm, v(-38916.04, 14463.18) * mm, v(-38941.71, 14456.3) * mm, v(-38967.39, 14449.47) * mm, v(-39001.63, 14440.4) * mm, v(-39044.43, 14429.18) * mm, v(-39112.89, 14411.44) * mm, v(-39232.67, 14380.95) * mm, v(-39403.7, 14338.92) * mm, v(-39608.72, 14290.74) * mm, v(-39813.44, 14244.62) * mm, v(-40017.8, 14200.37) * mm, v(-40221.74, 14157.82) * mm, v(-40492.97, 14103.08) * mm, v(-40830.57, 14037.98) * mm, v(-41232.83, 13963.75) * mm, v(-41631.67, 13892.03) * mm, v(-42026.5, 13821.48) * mm, v(-42416.75, 13750.8) * mm, v(-42801.8, 13678.73) * mm, v(-43181.09, 13604.04) * mm, v(-43553.98, 13525.56) * mm, v(-43919.87, 13442.14) * mm, v(-44278.17, 13352.7) * mm, v(-44628.32, 13256.2) * mm, v(-44969.77, 13151.62) * mm, v(-45302.07, 13038.02) * mm, v(-45571.01, 12935.04) * mm, v(-45781.24, 12847.21) * mm, v(-45936.43, 12778.5) * mm, v(-46089.1, 12706.83) * mm, v(-46214.23, 12644.54) * mm, v(-46313.07, 12593.1) * mm, v(-46386.57, 12553.71) * mm, v(-46459.44, 12513.49) * mm, v(-46519.65, 12479.25) * mm, v(-46567.5, 12451.43) * mm, v(-46603.23, 12430.35) * mm, v(-46632.87, 12412.6) * mm, v(-46656.5, 12398.28) * mm, v(-46674.19, 12387.5) * mm, v(-46691.84, 12376.64) * mm, v(-46709.47, 12365.72) * mm, v(-46727.08, 12354.74) * mm, v(-46750.52, 12340) * mm, v(-46779.77, 12321.42) * mm, v(-46826.48, 12291.32) * mm, v(-46884.68, 12253) * mm, v(-46954.24, 12205.92) * mm, v(-47023.51, 12157.75) * mm, v(-47092.5, 12108.5) * mm, v(-47161.23, 12058.16) * mm, v(-47252.5, 11989.6) * mm, v(-47411.27, 11865.9) * mm, v(-47635.51, 11678.56) * mm, v(-47900.62, 11437.23) * mm, v(-48161.86, 11179.86) * mm, v(-48419.37, 10907.02) * mm, v(-48673.22, 10619.36) * mm, v(-48923.54, 10317.56) * mm, v(-49170.46, 10002.34) * mm, v(-49414.1, 9674.47) * mm, v(-49654.66, 9334.73) * mm, v(-49892.3, 8983.91) * mm, v(-50127.24, 8622.84) * mm, v(-50359.71, 8252.33) * mm, v(-50666.71, 7746.82) * mm, v(-51045.58, 7095.47) * mm, v(-51494.74, 6289.27) * mm, v(-51940.99, 5465.03) * mm, v(-52238.37, 4907.83) * mm, v(-52387.53, 4628.36) * mm]});
            skLineSegment(sketch, "E12", {"start": v(-53265.33, 5096.84) * mm, "end": v(-52387.53, 4628.36) * mm});
            skLineSegment(sketch, "E13", {"start": v(-54796.66, -2444.5) * mm, "end": v(-53801.66, -2444.06) * mm});
            skSolve(sketch);
        }
        {
            var Q0;
            {var subQ0=sQuery(id+"F10.wireOp",EDGE,"E9");Q0=makeQuery(id+"F10.imprint","IMPRINT",FACE,{"disambiguationData":[TD([[makeQuery(id+"F10.imprint","IMPRINT",EDGE,{"derivedFrom":subQ0}),1.0]])]});}
            extrude(context, id + "F11", {"entities" : qUnion([Q0]), "operationType" : NewBodyOperationType.ADD, "depth" : 2000 * mm});
        }
        {
            var Q0;
            Q0=makeQuery(id+"F11.boolean.opBoolean","SPLIT",FACE,{"disambiguationData":[TD([makeQuery(id+"F5.opExtrude","SWEPT_FACE",FACE,{"disambiguationData":[OSD([sQuery(id+"F4.wireOp",EDGE,"E6.1")])]})])],"derivedFrom":makeQuery(id+"F3.opLoft","CAP_FACE",FACE,{"disambiguationData":[OSD([makeQuery(id+"F2.imprint","IMPRINT",FACE,{"disambiguationData":[TD([[makeQuery(id+"F2.imprint","IMPRINT",EDGE,{"derivedFrom":sQuery(id+"F2.wireOp",EDGE,"E2")}),1.0]])]})])],"isStart":true})});
            var sketch = newSketch(context, id + "F12", { "sketchPlane" : qUnion([Q0])});
            skCircle(sketch, "E14.cCircle", {"center": v(-2023.96, -17067.18) * mm, "radius": 4910.99 * mm, "construction": true});
            skLineSegment(sketch, "E14.0", {"start": v(-5878.63, -21226.34) * mm, "end": v(-7553.23, -15808.52) * mm});
            skLineSegment(sketch, "E14.1", {"start": v(-7553.23, -15808.52) * mm, "end": v(-3698.56, -11649.36) * mm});
            skLineSegment(sketch, "E14.2", {"start": v(-3698.56, -11649.36) * mm, "end": v(1830.7, -12908.03) * mm});
            skLineSegment(sketch, "E14.3", {"start": v(1830.7, -12908.03) * mm, "end": v(3505.3, -18325.85) * mm});
            skLineSegment(sketch, "E14.4", {"start": v(3505.3, -18325.85) * mm, "end": v(-349.36, -22485) * mm});
            skLineSegment(sketch, "E14.5", {"start": v(-349.36, -22485) * mm, "end": v(-5878.63, -21226.34) * mm});
            skPoint(sketch, "E14.0.midPoint", {"position": v(-6715.93, -18517.43) * mm});
            skSolve(sketch);
        }
        {
            var Q0;
            {var subQ6=sQuery(id+"F12.wireOp",EDGE,"E14.1");Q0=makeQuery(id+"F12.imprint","IMPRINT",FACE,{"disambiguationData":[TD([[makeQuery(id+"F12.imprint","IMPRINT",EDGE,{"derivedFrom":subQ6}),-1.0]])]});}
            extrude(context, id + "F13", {"entities" : qUnion([Q0]), "operationType" : NewBodyOperationType.ADD, "depth" : 5000 * mm});
        }
        {
            var Q0;
            Q0=makeQuery(id+"F13.opExtrude","CAP_FACE",FACE,{"disambiguationData":[OSD([sQuery(id+"F10.wireOp",EDGE,"E11.0"),sQuery(id+"F12.wireOp",EDGE,"E14.0"),sQuery(id+"F12.wireOp",EDGE,"E14.1"),sQuery(id+"F12.wireOp",EDGE,"E14.2"),sQuery(id+"F12.wireOp",EDGE,"E14.3"),sQuery(id+"F12.wireOp",EDGE,"E14.4")])],"isStart":false});
            var sketch = newSketch(context, id + "F14", { "sketchPlane" : qUnion([Q0])});
            skCircle(sketch, "E15.cCircle", {"center": v(-2005.13, -17119.24) * mm, "radius": 3961.73 * mm, "construction": true});
            skLineSegment(sketch, "E15.0", {"start": v(-692.44, -21501.47) * mm, "end": v(-5143.9, -20447.17) * mm});
            skLineSegment(sketch, "E15.1", {"start": v(-5143.9, -20447.17) * mm, "end": v(-6456.6, -16064.94) * mm});
            skLineSegment(sketch, "E15.2", {"start": v(-6456.6, -16064.94) * mm, "end": v(-3317.81, -12737) * mm});
            skLineSegment(sketch, "E15.3", {"start": v(-3317.81, -12737) * mm, "end": v(1133.65, -13791.3) * mm});
            skLineSegment(sketch, "E15.4", {"start": v(1133.65, -13791.3) * mm, "end": v(2446.34, -18173.53) * mm});
            skLineSegment(sketch, "E15.5", {"start": v(2446.34, -18173.53) * mm, "end": v(-692.44, -21501.47) * mm});
            skPoint(sketch, "E15.0.midPoint", {"position": v(-2918.17, -20974.32) * mm});
            skSolve(sketch);
        }
        {
            var Q0;
            Q0=makeQuery(id+"F14.imprint","IMPRINT",FACE,{"disambiguationData":[TD([[makeQuery(id+"F14.imprint","IMPRINT",EDGE,{"derivedFrom":sQuery(id+"F14.wireOp",EDGE,"E15.0")}),-1.0]])]});
            extrude(context, id + "F15", {"entities" : qUnion([Q0]), "operationType" : NewBodyOperationType.ADD, "depth" : 5000 * mm});
        }
        {
            var Q0;
            Q0=makeQuery(id+"F15.opExtrude","CAP_FACE",FACE,{"disambiguationData":[OSD([sQuery(id+"F14.wireOp",EDGE,"E15.0"),sQuery(id+"F14.wireOp",EDGE,"E15.1"),sQuery(id+"F14.wireOp",EDGE,"E15.2"),sQuery(id+"F14.wireOp",EDGE,"E15.3"),sQuery(id+"F14.wireOp",EDGE,"E15.4"),sQuery(id+"F14.wireOp",EDGE,"E15.5")])],"isStart":false});
            var sketch = newSketch(context, id + "F16", { "sketchPlane" : qUnion([Q0])});
            skCircle(sketch, "E16.cCircle", {"center": v(-1985.89, -17137.6) * mm, "radius": 3137.7 * mm, "construction": true});
            skLineSegment(sketch, "E16.0", {"start": v(1539.68, -17972.6) * mm, "end": v(-946.24, -20608.33) * mm});
            skLineSegment(sketch, "E16.1", {"start": v(-946.24, -20608.33) * mm, "end": v(-4471.8, -19773.33) * mm});
            skLineSegment(sketch, "E16.2", {"start": v(-4471.8, -19773.33) * mm, "end": v(-5511.46, -16302.6) * mm});
            skLineSegment(sketch, "E16.3", {"start": v(-5511.46, -16302.6) * mm, "end": v(-3025.54, -13666.86) * mm});
            skLineSegment(sketch, "E16.4", {"start": v(-3025.54, -13666.86) * mm, "end": v(500.03, -14501.86) * mm});
            skLineSegment(sketch, "E16.5", {"start": v(500.03, -14501.86) * mm, "end": v(1539.68, -17972.6) * mm});
            skPoint(sketch, "E16.0.midPoint", {"position": v(296.72, -19290.46) * mm});
            skSolve(sketch);
        }
        {
            var Q0;
            Q0=makeQuery(id+"F16.imprint","IMPRINT",FACE,{"disambiguationData":[TD([[makeQuery(id+"F16.imprint","IMPRINT",EDGE,{"derivedFrom":sQuery(id+"F16.wireOp",EDGE,"E16.0")}),-1.0]])]});
            extrude(context, id + "F17", {"entities" : qUnion([Q0]), "operationType" : NewBodyOperationType.ADD, "depth" : 5000 * mm});
        }
        {
            var Q0;
            Q0=makeQuery(id+"F11.boolean.opBoolean","SPLIT",FACE,{"disambiguationData":[TD([makeQuery(id+"F5.opExtrude","SWEPT_FACE",FACE,{"disambiguationData":[OSD([sQuery(id+"F4.wireOp",EDGE,"E6.1")])]})])],"derivedFrom":makeQuery(id+"F3.opLoft","CAP_FACE",FACE,{"disambiguationData":[OSD([makeQuery(id+"F2.imprint","IMPRINT",FACE,{"disambiguationData":[TD([[makeQuery(id+"F2.imprint","IMPRINT",EDGE,{"derivedFrom":sQuery(id+"F2.wireOp",EDGE,"E2")}),1.0]])]})])],"isStart":true})});
            var sketch = newSketch(context, id + "F18", { "sketchPlane" : qUnion([Q0])});
            skLineSegment(sketch, "E17", {"start": v(38472.8, 11123.54) * mm, "end": v(48414.9, 8758.93) * mm});
            skLineSegment(sketch, "E18", {"start": v(48414.9, 8758.93) * mm, "end": v(48414.9, -9351.8) * mm});
            skLineSegment(sketch, "E19", {"start": v(48414.9, -9351.8) * mm, "end": v(38687.77, -12038.85) * mm});
            skLineSegment(sketch, "E20", {"start": v(38687.77, -12038.85) * mm, "end": v(38472.8, 11123.54) * mm});
            skLineSegment(sketch, "E21", {"start": v(41697.27, 6770.51) * mm, "end": v(41824.97, -6989.5) * mm});
            skLineSegment(sketch, "E22", {"start": v(41824.97, -6989.5) * mm, "end": v(45781.59, -6181.08) * mm});
            skLineSegment(sketch, "E23", {"start": v(45781.59, -6181.08) * mm, "end": v(45666.86, 6181.3) * mm});
            skLineSegment(sketch, "E24", {"start": v(45666.86, 6181.3) * mm, "end": v(41697.27, 6770.51) * mm});
            skSolve(sketch);
        }
        {
            var Q0;
            Q0=makeQuery(id+"F18.imprint","IMPRINT",FACE,{"disambiguationData":[TD([[makeQuery(id+"F18.imprint","IMPRINT",EDGE,{"derivedFrom":sQuery(id+"F18.wireOp",EDGE,"E17")}),-1.0]])]});
            extrude(context, id + "F19", {"entities" : qUnion([Q0]), "operationType" : NewBodyOperationType.ADD, "depth" : 15000 * mm});
        }
        {
            var Q0;
            {var subQ3=makeQuery(id+"F5.opExtrude","SWEPT_FACE",FACE,{"disambiguationData":[OSD([sQuery(id+"F4.wireOp",EDGE,"E6.1")])]});Q0=makeQuery(id+"F19.boolean.opBoolean","SPLIT",FACE,{"disambiguationData":[TD([subQ3])],"derivedFrom":makeQuery(id+"F11.boolean.opBoolean","SPLIT",FACE,{"disambiguationData":[TD([subQ3])],"derivedFrom":makeQuery(id+"F3.opLoft","CAP_FACE",FACE,{"disambiguationData":[OSD([makeQuery(id+"F2.imprint","IMPRINT",FACE,{"disambiguationData":[TD([[makeQuery(id+"F2.imprint","IMPRINT",EDGE,{"derivedFrom":sQuery(id+"F2.wireOp",EDGE,"E2")}),1.0]])]})])],"isStart":true})})});}
            var sketch = newSketch(context, id + "F20", { "sketchPlane" : qUnion([Q0])});
            skLineSegment(sketch, "E25", {"start": v(-5642.8, 23893.09) * mm, "end": v(-7048.8, 15648.8) * mm});
            skLineSegment(sketch, "E26", {"start": v(-7048.8, 15648.8) * mm, "end": v(7720.63, 13129.98) * mm});
            skLineSegment(sketch, "E27", {"start": v(7720.63, 13129.98) * mm, "end": v(9104.6, 21245.09) * mm});
            skLineSegment(sketch, "E28", {"start": v(9104.6, 21245.09) * mm, "end": v(9104.6, 21667.1) * mm});
            skLineSegment(sketch, "E29", {"start": v(9104.6, 21667.1) * mm, "end": v(-5642.8, 23893.09) * mm});
            skSolve(sketch);
        }
        {
            var Q0;
            {var subQ0=sQuery(id+"F20.wireOp",EDGE,"E26");Q0=makeQuery(id+"F20.imprint","IMPRINT",FACE,{"disambiguationData":[TD([[makeQuery(id+"F20.imprint","IMPRINT",EDGE,{"derivedFrom":subQ0}),1.0]])]});}
            extrude(context, id + "F21", {"entities" : qUnion([Q0]), "operationType" : NewBodyOperationType.ADD, "depth" : 10000 * mm});
        }
        {
            var Q0;
            Q0=makeQuery(id+"F9.opExtrude","CAP_FACE",FACE,{"disambiguationData":[OSD([sQuery(id+"F8.wireOp",EDGE,"E8.0"),sQuery(id+"F8.wireOp",EDGE,"E8.1"),sQuery(id+"F8.wireOp",EDGE,"E8.2"),sQuery(id+"F8.wireOp",EDGE,"E8.3"),sQuery(id+"F8.wireOp",EDGE,"E8.4"),sQuery(id+"F8.wireOp",EDGE,"E8.5")])],"isStart":false});
            var sketch = newSketch(context, id + "F22", { "sketchPlane" : qUnion([Q0])});
            skCircle(sketch, "E30", {"center": v(-47468.93, 0) * mm, "radius": 5406.98 * mm});
            skSolve(sketch);
        }
        {
            var Q0;
            {var subQ0=makeQuery(id+"F9.opExtrude","CAP_EDGE",EDGE,{"disambiguationData":[OSD([sQuery(id+"F8.wireOp",EDGE,"E8.2")])],"isStart":false});Q0=makeQuery(id+"F22.imprint","IMPRINT",FACE,{"disambiguationData":[TD([[makeQuery(id+"F22.imprint","IMPRINT",EDGE,{"derivedFrom":subQ0}),-1.0]])]});}
            cPlane(context, id + "F23", {"entities" : qUnion([Q0]), "cplaneType" : CPlaneType.OFFSET, "offset" : 5000 * mm, "width" : 150 * mm, "height" : 150 * mm});
        }
        {
            var Q0;
            Q0=qCreatedBy(id+"F23.planeOp",FACE);
            var sketch = newSketch(context, id + "F24", { "sketchPlane" : qUnion([Q0])});
            skCircle(sketch, "E31", {"center": v(-47553.52, 0) * mm, "radius": 157.37 * mm});
            skSolve(sketch);
        }
        {
            var Q1;
            Q1=makeQuery(id+"F22.imprint","IMPRINT",FACE,{"disambiguationData":[TD([[makeQuery(id+"F22.imprint","IMPRINT",EDGE,{"derivedFrom":sQuery(id+"F22.wireOp",EDGE,"E30")}),1.0]])]});
            var Q2;
            Q2=sQuery(id+"F24.wireOp",VERTEX,"E31.center");
            loft(context, id + "F25", {"operationType" : NewBodyOperationType.ADD, "sheetProfilesArray" : [{ "sheetProfileEntities" : qUnion([Q1]) }, { "sheetProfileEntities" : qUnion([Q2]) }]});
        }
        {
            var Q0;
            Q0=makeQuery(id+"F21.opExtrude","CAP_FACE",FACE,{"disambiguationData":[OSD([sQuery(id+"F10.wireOp",EDGE,"E11.0"),sQuery(id+"F20.wireOp",EDGE,"E25"),sQuery(id+"F20.wireOp",EDGE,"E26"),sQuery(id+"F20.wireOp",EDGE,"E27")])],"isStart":false});
            var sketch = newSketch(context, id + "F26", { "sketchPlane" : qUnion([Q0])});
            skLineSegment(sketch, "E32", {"start": v(-5731.63, 23372.21) * mm, "end": v(-7048.8, 15648.8) * mm});
            skLineSegment(sketch, "E33", {"start": v(-7048.8, 15648.8) * mm, "end": v(7720.63, 13129.98) * mm});
            skLineSegment(sketch, "E34", {"start": v(7720.63, 13129.98) * mm, "end": v(9104.6, 21245.09) * mm});
            skLineSegment(sketch, "E35", {"start": v(9104.6, 21245.09) * mm, "end": v(-5731.63, 23372.21) * mm});
            skSolve(sketch);
        }
        {
            var Q0;
            Q0=makeQuery(id+"F26.imprint","IMPRINT",FACE,{"disambiguationData":[TD([[makeQuery(id+"F26.imprint","IMPRINT",EDGE,{"derivedFrom":sQuery(id+"F26.wireOp",EDGE,"E32")}),1.0]])]});
            cPlane(context, id + "F27", {"entities" : qUnion([Q0]), "cplaneType" : CPlaneType.OFFSET, "offset" : 3000 * mm, "width" : 150 * mm, "height" : 150 * mm});
        }
        {
            var Q0;
            Q0=qCreatedBy(id+"F27.planeOp",FACE);
            var sketch = newSketch(context, id + "F28", { "sketchPlane" : qUnion([Q0])});
            skLineSegment(sketch, "E36", {"start": v(-3411.27, 19396.13) * mm, "end": v(5695.65, 17974.23) * mm});
            skLineSegment(sketch, "E37", {"start": v(-3411.27, 19396.13) * mm, "end": v(-3423.15, 19320.03) * mm});
            skLineSegment(sketch, "E38", {"start": v(-3423.15, 19320.03) * mm, "end": v(5695.65, 17950.39) * mm});
            skLineSegment(sketch, "E39", {"start": v(5695.65, 17950.39) * mm, "end": v(5695.65, 17974.23) * mm});
            skSolve(sketch);
        }
        {
            var Q1;
            Q1=makeQuery(id+"F26.imprint","IMPRINT",FACE,{"disambiguationData":[TD([[makeQuery(id+"F26.imprint","IMPRINT",EDGE,{"derivedFrom":sQuery(id+"F26.wireOp",EDGE,"E32")}),1.0]])]});
            var Q2;
            Q2=makeQuery(id+"F28.imprint","IMPRINT",FACE,{"disambiguationData":[TD([[makeQuery(id+"F28.imprint","IMPRINT",EDGE,{"derivedFrom":sQuery(id+"F28.wireOp",EDGE,"E36")}),-1.0]])]});
            loft(context, id + "F29", {"operationType" : NewBodyOperationType.ADD, "sheetProfilesArray" : [{ "sheetProfileEntities" : qUnion([Q1]) }, { "sheetProfileEntities" : qUnion([Q2]) }]});
        }
    });
